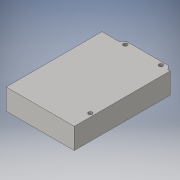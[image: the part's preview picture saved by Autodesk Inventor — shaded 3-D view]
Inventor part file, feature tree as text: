
AUTODESK INVENTOR PART (.ipt)
format: ipt  version: 2016 (Build 200138000, 138)  size: 130,048 bytes
history: native  units: in
note: dims shown in document units (in); Inventor stores cm internally (conversion verified against a paired STEP export)
features: extrude x2, chamfer x1, sketch x1
ambient origin geometry x8: Origin, YZ Plane, XZ Plane, XY Plane, X Axis, Y Axis, Z Axis, Center Point
bodies: Solid1 (feature_tree)
feature tree (4):
  extrude  "Extrusion1"  Depth=2.103in
  chamfer  "Chamfer1"  Distance=1.473in
  extrude  "Extrusion2"  Depth=0.08in
  sketch  "Sketch1"  dims[d0=2.958in d1=2.103in d2=1.473in d3=0.08in d4=0.116in d5=0.647in d6=0.0in d7=0.1in d8=0.125in d9=45.0deg d10=0.121in d11=0.1035in d12=0.121in d13=0.1035in d14=0.2965in d15=1.098in d16=0.599in d17=0.104in d18=0.121in d19=0.647in d20=0.0in d21=2.3715in d22=0.1925in d24=2.3793in d25=2.958in d26=2.103in d27=0.08in d29=0.116in d30=1.4717in d31=0.116in d32=0.55in d33=2.958in]
